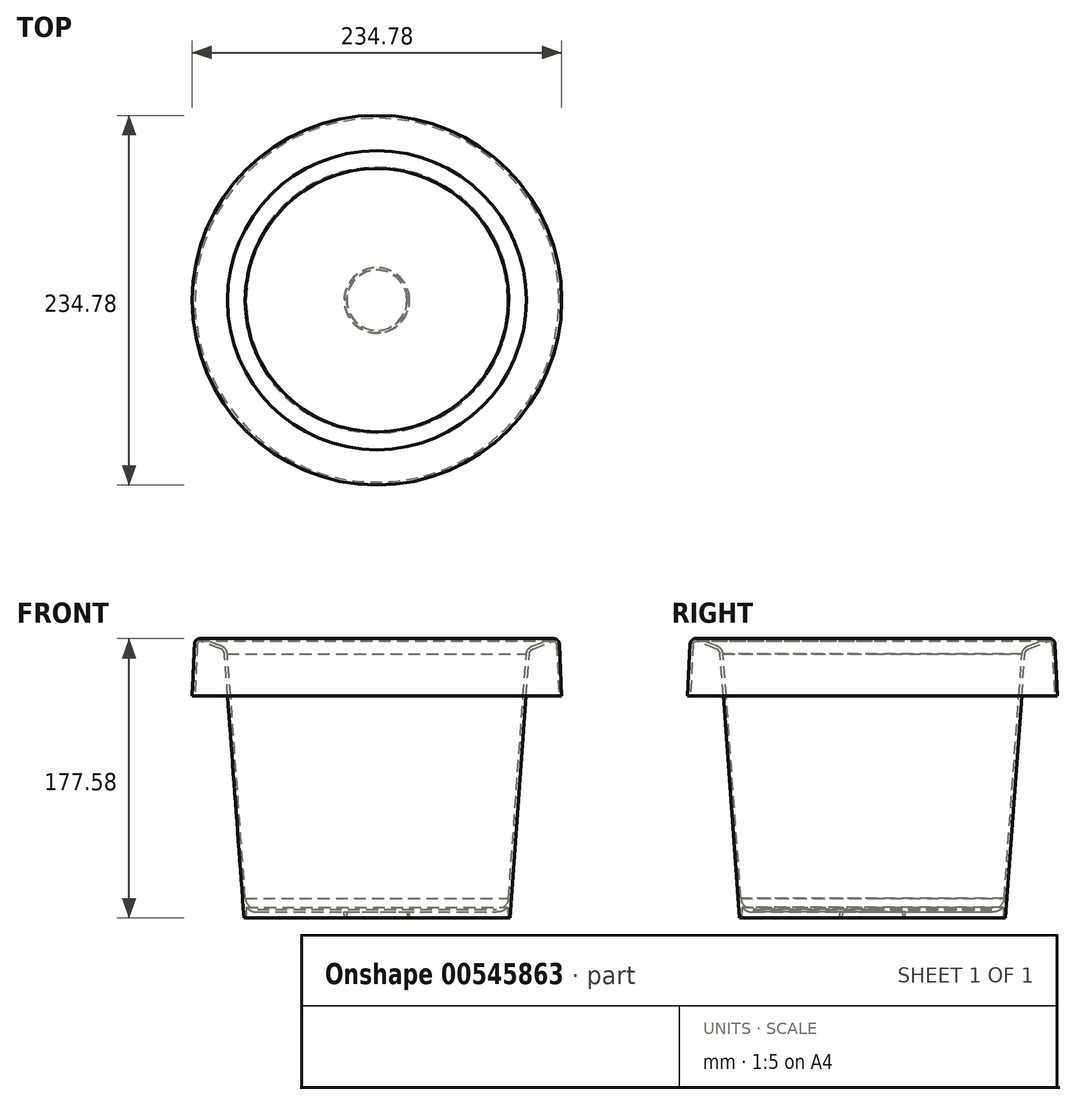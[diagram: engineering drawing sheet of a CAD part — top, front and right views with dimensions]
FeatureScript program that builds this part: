
annotation { "Feature Type Name" : "Feature", "Feature Type Description" : "" }
export const myFeature = defineFeature(function(context is Context, id is Id, definition is map)
    precondition{}
    {
        {
            var Q0;
            Q0=qCreatedBy(makeId("Front.planeOp"),FACE);
            var sketch = newSketch(context, id + "F0", { "sketchPlane" : qUnion([Q0])});
            skLineSegment(sketch, "E0", {"start": v(20.57, -3.81) * mm, "end": v(19.3, -3.81) * mm});
            skLineSegment(sketch, "E1", {"start": v(19.3, -3.81) * mm, "end": v(19.05, 0) * mm});
            skLineSegment(sketch, "E2", {"start": v(20.83, 0) * mm, "end": v(20.57, -3.81) * mm});
            skLineSegment(sketch, "E3", {"start": v(0, -3.81) * mm, "end": v(0, 0) * mm});
            skLineSegment(sketch, "E4", {"start": v(0, 0) * mm, "end": v(19.05, 0) * mm});
            skLineSegment(sketch, "E5", {"start": v(0, 0) * mm, "end": v(0, 1.78) * mm});
            skLineSegment(sketch, "E6", {"start": v(0, -3.81) * mm, "end": v(0, 175.26) * mm});
            skLineSegment(sketch, "E7", {"start": v(0, -3.81) * mm, "end": v(0, 167.64) * mm});
            skLineSegment(sketch, "E8", {"start": v(115.61, 137.16) * mm, "end": v(117.39, 137.16) * mm});
            skArc(sketch, "E9", {"start": v(114.07, 170.2) * mm, "mid": v(113.24, 171.66) * mm, "end": v(111.58, 171.85) * mm});
            skLineSegment(sketch, "E10", {"start": v(114.07, 170.2) * mm, "end": v(115.61, 137.16) * mm});
            skLineSegment(sketch, "E11", {"start": v(115.85, 170.28) * mm, "end": v(117.39, 137.16) * mm});
            skArc(sketch, "E12", {"start": v(99.32, 167.27) * mm, "mid": v(97.55, 165.93) * mm, "end": v(96.78, 163.84) * mm});
            skLineSegment(sketch, "E13", {"start": v(99.32, 167.27) * mm, "end": v(111.58, 171.85) * mm});
            skLineSegment(sketch, "E14", {"start": v(110.95, 173.54) * mm, "end": v(98.68, 168.95) * mm});
            skArc(sketch, "E15", {"start": v(98.68, 168.95) * mm, "mid": v(96.1, 167) * mm, "end": v(95, 163.96) * mm});
            skLineSegment(sketch, "E16", {"start": v(117.39, 137.16) * mm, "end": v(0, 137.16) * mm, "construction": true});
            skLineSegment(sketch, "E17", {"start": v(95, 163.96) * mm, "end": v(0, 163.96) * mm, "construction": true});
            skLineSegment(sketch, "E18", {"start": v(0, 173.54) * mm, "end": v(0, 175.32) * mm});
            skLineSegment(sketch, "E19", {"start": v(116.17, 163.32) * mm, "end": v(117.95, 163.32) * mm, "construction": true});
            skLineSegment(sketch, "E20", {"start": v(116.17, 163.32) * mm, "end": v(117.95, 163.32) * mm});
            skPoint(sketch, "E21.orphan", {"position": v(120.29, 163.32) * mm});
            skPoint(sketch, "E22.orphan", {"position": v(115.61, 163.32) * mm});
            skLineSegment(sketch, "E23", {"start": v(117.62, 170.29) * mm, "end": v(117.95, 163.32) * mm, "construction": true});
            skLineSegment(sketch, "E24", {"start": v(117.95, 163.32) * mm, "end": v(117.62, 170.29) * mm});
            skPoint(sketch, "E25.start.orphan", {"position": v(115.7, 173.74) * mm});
            skArc(sketch, "E26", {"start": v(117.62, 170.29) * mm, "mid": v(115.94, 173.88) * mm, "end": v(112.22, 175.26) * mm});
            skArc(sketch, "E27", {"start": v(115.85, 170.28) * mm, "mid": v(114.23, 173.16) * mm, "end": v(110.95, 173.54) * mm});
            skLineSegment(sketch, "E28", {"start": v(112.22, 173.77) * mm, "end": v(0, 173.77) * mm, "construction": true});
            skLineSegment(sketch, "E29", {"start": v(0, 1.78) * mm, "end": v(60.2, 1.78) * mm});
            skLineSegment(sketch, "E30", {"start": v(20.83, 0) * mm, "end": v(60.24, 0) * mm});
            skLineSegment(sketch, "E31", {"start": v(0, -3.81) * mm, "end": v(84.46, -3.81) * mm, "construction": true});
            skLineSegment(sketch, "E32", {"start": v(96.78, 163.84) * mm, "end": v(85.37, 8.7) * mm});
            skLineSegment(sketch, "E33", {"start": v(84.45, -3.81) * mm, "end": v(83.19, -3.81) * mm});
            skLineSegment(sketch, "E34", {"start": v(83.04, 1.78) * mm, "end": v(83.19, -3.81) * mm});
            skLineSegment(sketch, "E35", {"start": v(92.9, 137.16) * mm, "end": v(95, 163.96) * mm});
            skLineSegment(sketch, "E36", {"start": v(82.3, 1.78) * mm, "end": v(82.3, 1.77) * mm});
            skLineSegment(sketch, "E37", {"start": v(75.93, 1.78) * mm, "end": v(60.2, 1.78) * mm});
            skLineSegment(sketch, "E38.trimOffspring", {"start": v(84.87, 1.78) * mm, "end": v(84.45, -3.81) * mm});
            skArc(sketch, "E39", {"start": v(75.93, 0) * mm, "mid": v(79.8, 0.8) * mm, "end": v(83, 3.12) * mm});
            skLineSegment(sketch, "E40", {"start": v(85.37, 8.7) * mm, "end": v(84.87, 1.78) * mm});
            skLineSegment(sketch, "E41", {"start": v(83.19, -3.81) * mm, "end": v(83, 3.12) * mm});
            skLineSegment(sketch, "E42", {"start": v(83.6, 8.83) * mm, "end": v(92.9, 137.16) * mm});
            skArc(sketch, "E43", {"start": v(75.93, 1.78) * mm, "mid": v(81.14, 3.8) * mm, "end": v(83.6, 8.83) * mm});
            skLineSegment(sketch, "E44", {"start": v(60.24, 0) * mm, "end": v(75.93, 0) * mm});
            skSolve(sketch);
        }
        {
            var Q0;
            Q0=makeQuery(id+"F0.imprint","IMPRINT",FACE,{"disambiguationData":[TD([[makeQuery(id+"F0.imprint","IMPRINT",EDGE,{"derivedFrom":sQuery(id+"F0.wireOp",EDGE,"E0")}),-1.0]])]});
            var Q1;
            Q1=sQuery(id+"F0.wireOp",EDGE,"E7");
            revolve(context, id + "F1", {"entities" : qUnion([Q0]), "axis" : qUnion([Q1]), "revolveType" : RevolveType.FULL});
        }
    });
